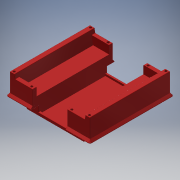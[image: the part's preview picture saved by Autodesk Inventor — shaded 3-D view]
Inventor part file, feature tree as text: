
AUTODESK INVENTOR PART (.ipt)
format: ipt  version: 2018 (Build 220112000, 112)  size: 791,552 bytes
history: native  units: in
note: dims shown in document units (in); Inventor stores cm internally (conversion verified against a paired STEP export)
features: sketch x13, extrude x11, revolve x4, projected_geometry x4, plane x3, fillet x3, hole x1, mirror x1, other x1
ambient origin geometry x8: Origin, YZ Plane, XZ Plane, XY Plane, X Axis, Y Axis, Z Axis, Center Point
bodies: Solid1 (feature_tree)
feature tree (41):
  extrude  "Extrusion1"  Depth=0.6871in
  extrude  "Extrusion3"  TaperAngle=150.0deg  [1 undecoded]
  plane  "Work Plane1"
  extrude  "Extrusion4"  Depth=2.5in
  extrude  "Extrusion5"  Depth=44.0in
  extrude  "Extrusion6"  Depth=5.0in
  extrude  "Extrusion7"  Depth=84.0in TaperAngle=0.0deg
  plane  "Work Plane2"
  extrude  "Extrusion8"  Depth=2.5in
  extrude  "Extrusion9"  Depth=2.5in
  sketch  "Sketch10"  dims[d64=0.7874in d66=80.0in d67=0.7874in d69=79.0in d72=2.5in]
  revolve  "Revolution1"  [1 undecoded]
  revolve  "Revolution2"  [1 undecoded]
  sketch  "Sketch11"  dims[d73=2.0in d74=21.0in]
  revolve  "Revolution3"  [1 undecoded]
  revolve  "Revolution4"  [1 undecoded]
  extrude  "Extrusion10"  Depth=2.0in
  plane  "Work Plane4"
  extrude  "Extrusion11"  Depth=2.0in TaperAngle=0.0deg
  fillet  "Fillet1"  Radius=24.0in
  fillet  "Fillet2"  Radius=36.0in
  fillet  "Fillet3"  Radius=18.25in
  hole  "Hole1"  [1 undecoded]
  mirror  "Mirror1"
  extrude  "Extrusion12"  Depth=2.0in TaperAngle=0.0deg
  sketch  "Sketch1"  dims[d5=84.0in d11=0.6871in]
  other  "Image1"
  sketch  "Sketch3"  dims[d17=1.0994in d20=150.0deg]
  sketch  "Sketch4"  dims[d30=34.0in d31=2.5in]
  sketch  "Sketch5"  dims[d33=19.5in d34=44.0in]
  sketch  "Sketch6"  dims[d35=8.25in d44=5.0in]
  sketch  "Sketch7"  dims[d46=24.0in d53=84.0in d54=0.0in]
  sketch  "Sketch8"  dims[d56=5.0in d61=2.5in]
  sketch  "Sketch9"  dims[d62=2.0in d63=2.5in]
  projected_geometry  "Projected Loop3"
  projected_geometry  "Projected Loop4"
  projected_geometry  "Projected Loop5"
  projected_geometry  "Projected Loop6"
  sketch  "Sketch12"  dims[d75=0.7874in d77=80.0in d78=0.7874in d80=42.0in d83=8.0in d84=0.0in]
  sketch  "Sketch14"  dims[d85=-6.0in d86=16.75in]
  sketch  "Sketch15"  dims[d87=8.5069in d88=15.4931in d89=72.0in d90=0.0in d93=24.0in d94=36.0in d95=18.25in d96=84.0in d98=6.0in d99=0.0in d100=84.0in d101=6.0in d102=0.0in d103=1.0994in d104=150.0deg d105=1.0994in d106=150.0deg d107=6.0in d108=0.0in d109=-42.0in d110=3.0in d111=2.5in d112=84.0in d113=0.0in d114=2.5in d115=3.0in d116=84.0in d117=0.0in d118=90.0deg d119=90.0deg d120=90.0deg d121=90.0deg d122=84.0in d123=0.0in d124=0.5in d125=0.5in d126=0.5in d128=-42.0in d129=76.0in d130=0.0in d131=2.0in d132=2.0in d133=2.0in d134=10.0in d135=2.5in d136=0.417in d137=1.0in d138=0.375in d139=0.25in d140=0.5635in d141=1.385in d142=0.8108in d143=68.0in d144=36.0in d145=2.0in d146=0.0in]
note: 6 required parameter values undecoded (feature->parameter linkage not recoverable at this tier; creation-order binding heuristic only, values carry confidence <= 0.55)